# Revit family: חלון פלדה דו כנפי וחלון אלומיניום דריי קיפ
name_source: partatom
category: Windows
units: mm (PartAtom-declared; Revit-internal decimal feet)

## family parameters
Always vertical = Yes
Cut with Voids When Loaded = No
Host = Wall
Room Calculation Point = No
Shared = No

## types (1)
- חלון מרחב מוגן
    Analytic Construction = <None>
    Default Sill Height = 1080 mm  [stored 3.54331 ft]
    Define Thermal Properties by = Schematic Type
    Heght actual = 800 mm  [stored 2.62467 ft]
    Height = 800 mm  [stored 2.62467 ft]
    Wall Closure = By host
    Width = 800 mm  [stored 2.62467 ft]
    Width actual = 800 mm  [stored 2.62467 ft]
    rohav klali = 327 mm
    rohav plata yahasi = 130 mm  [stored 0.426509 ft]
    גובה = 1200 mm
    חומר = Default
    פתיחה = 800 mm  [stored 2.62467 ft]

note: [stored X ft] marks values corroborated as IEEE doubles in the binary element streams (Revit-internal decimal feet)

## geometry (parser evidence)
native form markers: Blend x3, Sweep x3
no freeform markers — native parametric forms only
